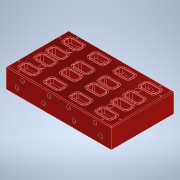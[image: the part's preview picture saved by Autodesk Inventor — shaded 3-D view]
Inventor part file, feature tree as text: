
AUTODESK INVENTOR PART (.ipt)
format: ipt  version: 2022 (Build 260153000, 153)  size: 909,824 bytes
history: native  units: mm
features: hole x6, other x5, extrude x4, sketch x4, chamfer x1
ambient origin geometry x8: Origin, YZ Plane, XZ Plane, XY Plane, X Axis, Y Axis, Z Axis, Center Point
bodies: Volumenkörper1 (feature_tree)
feature tree (20):
  other  "Annotations"
  extrude  "Extrusion1"  Depth=139.7mm
  chamfer  "Fase1"  Distance=44.45mm
  other  "Alignment Holes"
  hole  "Bohrung7"  [1 undecoded]
  other  "Wells"
  extrude  "Extrusion6"  Depth=5.0mm
  extrude  "Extrusion7"  Depth=35.56mm
  sketch  "Sketch17"  dims[d11=2.0mm d12=2.0mm d13=45.0deg d153=24.0mm]
  hole  "Hole12"  [1 undecoded]
  hole  "Hole13"  [1 undecoded]
  sketch  "Sketch19"  dims[d154=24.0mm d155=5.0mm]
  hole  "Hole15"  [1 undecoded]
  hole  "Hole16"  [1 undecoded]
  hole  "Hole18"  [1 undecoded]
  extrude  "Extrusion9"  Depth=35.56mm
  sketch  "Skizze1"  dims[d0=234.95mm d2=139.7mm d3=44.45mm d4=0.0mm]
  sketch  "Sketch22"  dims[d156=5.0mm d157=24.0mm d158=5.0mm d159=5.0mm d160=24.0mm d161=24.0mm d162=5.0mm d163=5.0mm d164=24.0mm d165=5.0mm d166=24.0mm d167=5.0mm d168=24.0mm d169=3.242mm d170=6.0mm d171=8.0mm d172=4.6mm d173=14.3117mm d174=20.0mm d175=20.594885mm d259=30.0mm d260=15.0mm d261=8.5mm d262=11.5mm d266=3.0mm d267=40.0mm d269=57.317mm d270=20.0mm d272=35.566mm d276=11.499mm d277=10.0mm d278=0.0mm d279=30.0mm d280=0.0mm d283=10.0mm d284=20.0mm d286=59.317mm d287=10.0mm d289=10.0mm d291=7.9502mm d292=6.92404mm d293=0.624793mm d294=8.304022mm d295=4.0mm d296=2.0mm d297=90.0deg d298=20.0mm d299=20.594885mm d300=7.9502mm d301=6.92404mm d302=0.624793mm d303=8.304022mm d304=4.0mm d305=2.0mm d306=90.0deg d307=55.0mm d308=20.594885mm d326=20.0mm d328=59.317mm d329=10.0mm d331=10.0mm d333=7.9502mm d334=6.92404mm d335=0.624793mm d336=8.304022mm d337=4.0mm d338=2.0mm d339=90.0deg d340=55.0mm d341=20.594885mm d342=7.9502mm d343=6.92404mm d344=0.624793mm d345=8.304022mm d346=4.0mm d347=2.0mm d348=90.0deg d349=20.0mm d350=20.594885mm d382=76.2mm d383=152.4mm d384=31.0mm d385=62.0mm d386=6.7564mm d387=6.0mm d388=11.1252mm d389=6.35mm d390=14.3117mm d391=8.0mm d392=20.594885mm d410=11.5mm d411=8.5mm d412=15.0mm d413=30.0mm d414=3.0mm d415=40.0mm d417=57.317mm d418=20.0mm d420=35.566mm d441=2.38125mm d442=0.0mm d443=10.0mm d444=10.0mm d446=12.5mm d447=12.5mm d448=12.5mm d449=12.5mm d450=20.0mm d451=12.5mm d452=12.5mm d453=1.27mm d454=1.27mm d455=1.27mm d456=1.27mm d457=3.175mm d458=3.175mm d459=3.175mm d460=3.175mm d468=40.0mm d470=57.3278mm d471=20.0mm d473=35.56mm]
  other  "Seal Seating"
  other  "General Note 1"
note: 6 required parameter values undecoded (feature->parameter linkage not recoverable at this tier; creation-order binding heuristic only, values carry confidence <= 0.55)
